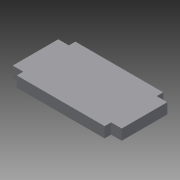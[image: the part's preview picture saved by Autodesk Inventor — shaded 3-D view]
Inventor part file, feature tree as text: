
AUTODESK INVENTOR PART (.ipt)
format: ipt  version: 2013 (Build 170138000, 138)  size: 97,792 bytes
history: native  units: mm
features: other x2, extrude x1, sketch x1
ambient origin geometry x8: Origin, YZ Plane, XZ Plane, XY Plane, X Axis, Y Axis, Z Axis, Center Point
feature tree (4):
  other  "Blocks"
  extrude  "Extrusion6"  Depth=3.0mm
  sketch  "Sketch1"  dims[d0=3.0mm d2=3.0mm d3=0.1mm d7=22.5mm d8=12.4mm d9=4.5mm d10=4.5mm d11=2.0mm d12=2.0mm d42=27.0mm d43=18.0mm d44=3.25mm d45=14.0mm d46=3.25mm d47=0.0mm]
  other  "Block1"
